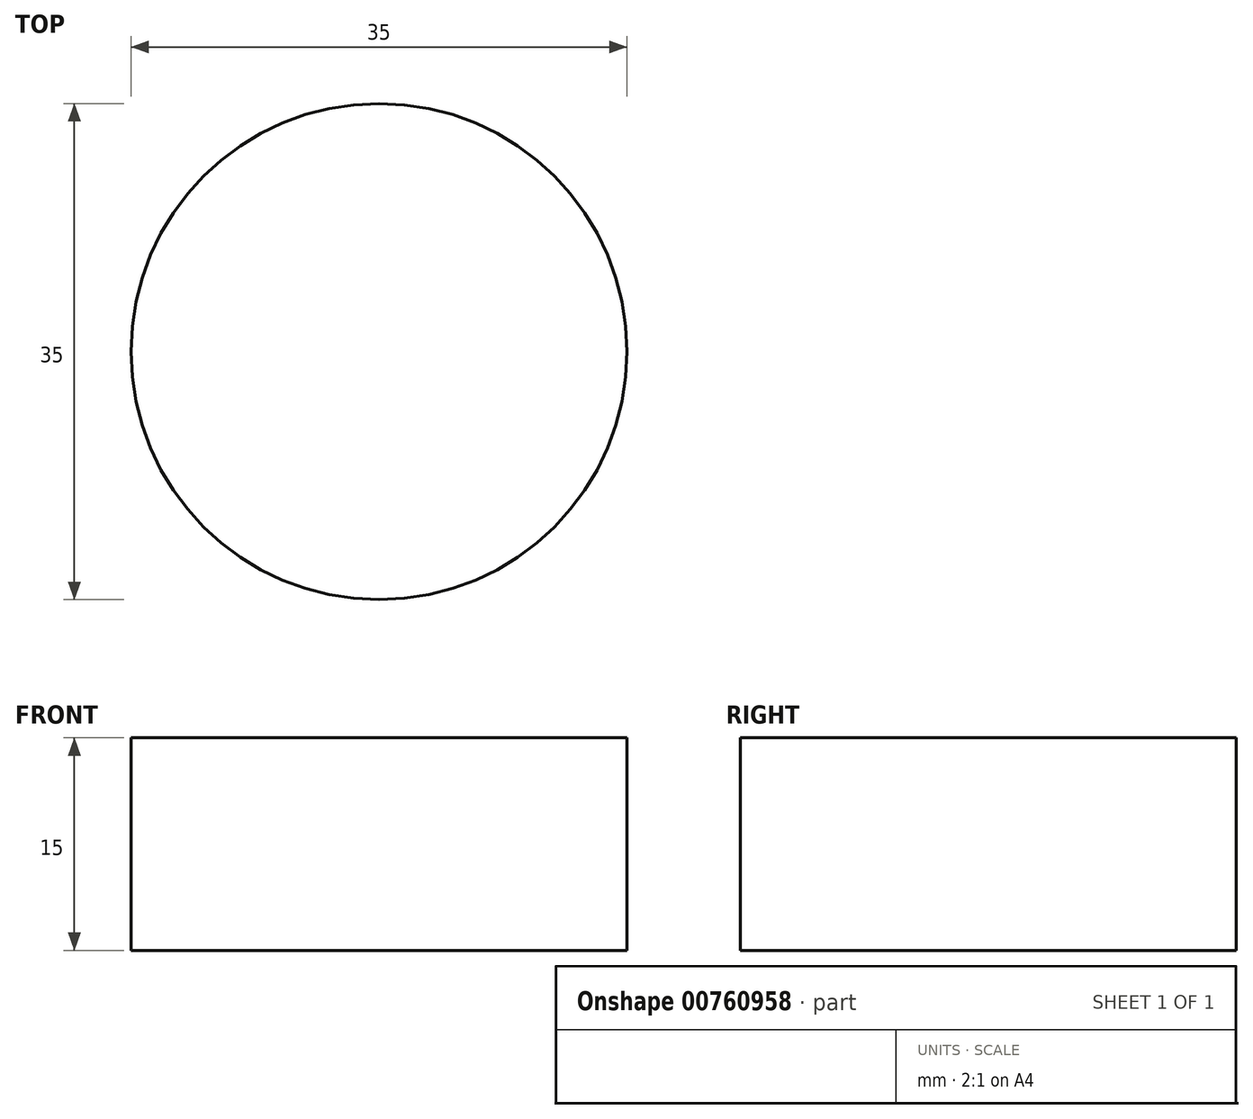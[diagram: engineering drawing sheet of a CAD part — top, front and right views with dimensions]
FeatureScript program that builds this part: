
annotation { "Feature Type Name" : "Feature", "Feature Type Description" : "" }
export const myFeature = defineFeature(function(context is Context, id is Id, definition is map)
    precondition{}
    {
        {
            var Q0;
            Q0=qCreatedBy(makeId("Top.planeOp"),FACE);
            var sketch = newSketch(context, id + "F0", { "sketchPlane" : qUnion([Q0])});
            skCircle(sketch, "E0", {"center": v(0, 0) * mm, "radius": 17.5 * mm});
            skSolve(sketch);
        }
        {
            var Q0;
            Q0 = qSketchRegion(id + "F0", true);
            extrude(context, id + "F1", {"entities" : qUnion([Q0]), "depth" : 15 * mm, "offsetDistance" : 25 * mm});
        }
    });
